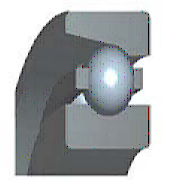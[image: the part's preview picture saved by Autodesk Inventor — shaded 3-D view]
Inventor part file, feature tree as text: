
AUTODESK INVENTOR PART (.ipt)
format: ipt  version: 2018 (Build 220112000, 112)  size: 426,496 bytes
history: native  units: mm
features: sketch x2
ambient origin geometry x8: Origin, YZ Plane, XZ Plane, XY Plane, X Axis, Y Axis, Z Axis, Center Point
bodies: Solid1 (feature_tree)
feature tree (2):
  sketch  "Sketch1"  dims[d1=30.0mm]
  sketch  "Sketch2"  dims[d2=6.6mm d3=17.0mm d5=15.0deg d8=3.38mm d20=1.745329mm d24=6.65mm d35=0.3mm d36=0.15mm d37=0.15mm d38=21.238mm d39=25.762mm d40=22.1428mm d41=0.3mm d42=7.0mm d43=3.38mm d44=15.0deg d46=90.0deg d47=90.0deg d48=110.0mm d49=360.0deg d51=0.0mm d52=0.0mm d53=0.0mm d54=0.0mm d55=0.0mm]
